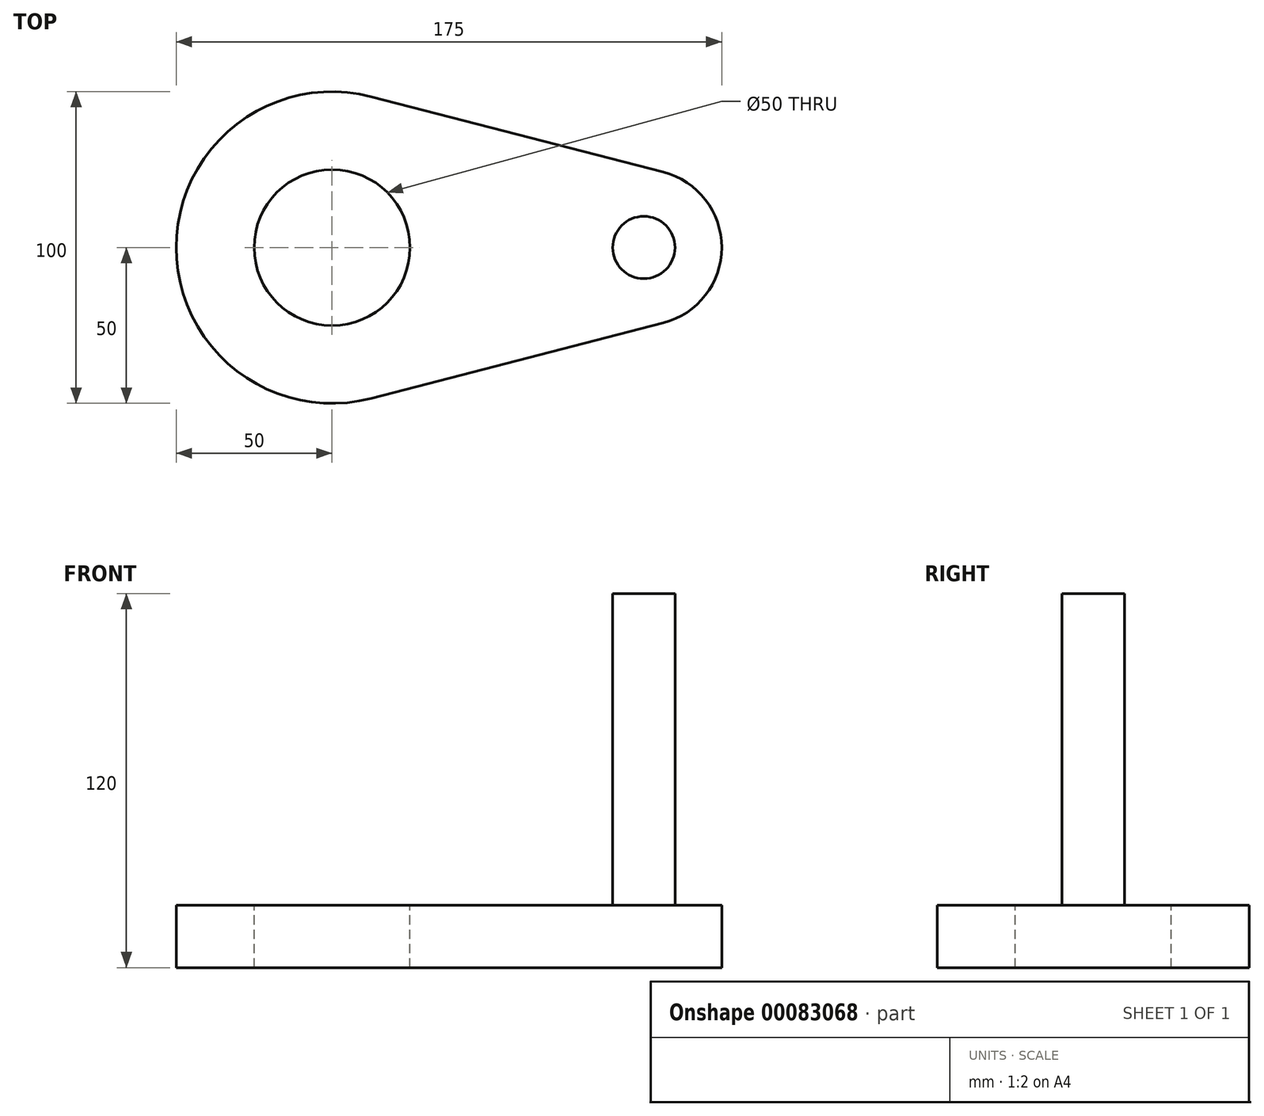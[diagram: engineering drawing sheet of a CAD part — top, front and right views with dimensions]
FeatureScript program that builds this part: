
annotation { "Feature Type Name" : "Feature", "Feature Type Description" : "" }
export const myFeature = defineFeature(function(context is Context, id is Id, definition is map)
    precondition{}
    {
        {
            var Q0;
            Q0=qCreatedBy(makeId("Top.planeOp"),FACE);
            var sketch = newSketch(context, id + "F0", { "sketchPlane" : qUnion([Q0])});
            skCircle(sketch, "E0", {"center": v(0, 0) * mm, "radius": 50 * mm});
            skCircle(sketch, "E1", {"center": v(100, 0) * mm, "radius": 25 * mm});
            skLineSegment(sketch, "E2", {"start": v(12.5, 48.41) * mm, "end": v(106.25, 24.2) * mm});
            skLineSegment(sketch, "E3", {"start": v(12.5, -48.41) * mm, "end": v(106.25, -24.2) * mm});
            skLineSegment(sketch, "E4", {"start": v(0, 0) * mm, "end": v(100, 0) * mm});
            skSolve(sketch);
        }
        {
            var Q0;
            {var subQ0=sQuery(id+"F0.wireOp",EDGE,"E0");var subQ1=makeQuery(id+"F0.imprint","INTERSECT",VERTEX,{"derivedFrom":[subQ0,sQuery(id+"F0.wireOp",EDGE,"E2")]});Q0=makeQuery(id+"F0.imprint","IMPRINT",FACE,{"disambiguationData":[TD([[makeQuery(id+"F0.imprint","IMPRINT",EDGE,{"disambiguationData":[TD([[subQ1,1.0]])],"derivedFrom":subQ0}),1.0]])]});}
            var Q1;
            {var subQ0=sQuery(id+"F0.wireOp",EDGE,"E2");Q1=makeQuery(id+"F0.imprint","IMPRINT",FACE,{"disambiguationData":[TD([[makeQuery(id+"F0.imprint","IMPRINT",EDGE,{"derivedFrom":subQ0}),-1.0]])]});}
            var Q2;
            {var subQ0=sQuery(id+"F0.wireOp",EDGE,"E3");Q2=makeQuery(id+"F0.imprint","IMPRINT",FACE,{"disambiguationData":[TD([[makeQuery(id+"F0.imprint","IMPRINT",EDGE,{"derivedFrom":subQ0}),1.0]])]});}
            var Q3;
            {var subQ0=sQuery(id+"F0.wireOp",EDGE,"E1");var subQ1=makeQuery(id+"F0.imprint","INTERSECT",VERTEX,{"derivedFrom":[subQ0,sQuery(id+"F0.wireOp",EDGE,"E2")]});Q3=makeQuery(id+"F0.imprint","IMPRINT",FACE,{"disambiguationData":[TD([[makeQuery(id+"F0.imprint","IMPRINT",EDGE,{"disambiguationData":[TD([[subQ1,-1.0]])],"derivedFrom":subQ0}),1.0]])]});}
            extrude(context, id + "F1", {"entities" : qUnion([Q0, Q1, Q2, Q3]), "depth" : 20 * mm});
        }
        {
            var Q0;
            Q0=makeQuery(id+"F1.opExtrude","CAP_FACE",FACE,{"disambiguationData":[OSD([sQuery(id+"F0.wireOp",EDGE,"E0"),sQuery(id+"F0.wireOp",EDGE,"E1"),sQuery(id+"F0.wireOp",EDGE,"E2"),sQuery(id+"F0.wireOp",EDGE,"E3")])],"isStart":false});
            var sketch = newSketch(context, id + "F3", { "sketchPlane" : qUnion([Q0])});
            skCircle(sketch, "E5", {"center": v(0, 0) * mm, "radius": 25 * mm});
            skSolve(sketch);
        }
        {
            var Q0;
            Q0=makeQuery(id+"F3.imprint","IMPRINT",FACE,{"disambiguationData":[TD([[makeQuery(id+"F3.imprint","IMPRINT",EDGE,{"derivedFrom":sQuery(id+"F3.wireOp",EDGE,"E5")}),1.0]])]});
            extrude(context, id + "F2", {"entities" : qUnion([Q0]), "operationType" : NewBodyOperationType.REMOVE, "endBound" : BoundingType.THROUGH_ALL, "oppositeDirection" : true, "depth" : 25 * mm});
        }
        {
            var Q0;
            Q0=makeQuery(id+"F1.opExtrude","CAP_FACE",FACE,{"disambiguationData":[OSD([sQuery(id+"F0.wireOp",EDGE,"E0"),sQuery(id+"F0.wireOp",EDGE,"E1"),sQuery(id+"F0.wireOp",EDGE,"E2"),sQuery(id+"F0.wireOp",EDGE,"E3")])],"isStart":false});
            var sketch = newSketch(context, id + "F4", { "sketchPlane" : qUnion([Q0])});
            skCircle(sketch, "E6", {"center": v(100, 0) * mm, "radius": 10 * mm});
            skSolve(sketch);
        }
        {
            var Q0;
            Q0=makeQuery(id+"F4.imprint","IMPRINT",FACE,{"disambiguationData":[TD([[makeQuery(id+"F4.imprint","IMPRINT",EDGE,{"derivedFrom":sQuery(id+"F4.wireOp",EDGE,"E6")}),1.0]])]});
            extrude(context, id + "F5", {"entities" : qUnion([Q0]), "operationType" : NewBodyOperationType.ADD, "depth" : 100 * mm});
        }
    });
